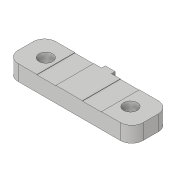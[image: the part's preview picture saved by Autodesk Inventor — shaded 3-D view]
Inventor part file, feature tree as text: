
AUTODESK INVENTOR PART (.ipt)
format: ipt  version: 2020 (Build 240168000, 168)  size: 139,776 bytes
history: native  units: in
note: dims shown in document units (in); Inventor stores cm internally (conversion verified against a paired STEP export)
features: extrude x5, sketch x5, mirror x2, plane x1, fillet x1
ambient origin geometry x8: Origin, YZ Plane, XZ Plane, XY Plane, X Axis, Y Axis, Z Axis, Center Point
bodies: Solid1 (feature_tree)
feature tree (14):
  extrude  "Extrusion1"  Depth=0.3937in
  extrude  "Extrusion2"  Depth=0.1575in TaperAngle=0.0deg
  plane  "Work Plane1"
  mirror  "Mirror1"
  fillet  "Fillet1"  [1 undecoded]
  extrude  "Extrusion3"  Depth=0.1181in
  extrude  "Extrusion4"  Depth=0.3937in
  mirror  "Mirror2"
  extrude  "Extrusion6"  Depth=0.315in
  sketch  "Sketch1"  dims[d0=1.2992in d1=0.3937in]
  sketch  "Sketch2"  dims[d2=0.1575in d3=0.0in d5=0.1575in d6=0.0in d7=-0.6496in]
  sketch  "Sketch3"  dims[d8=0.1181in d9=0.1417in]
  sketch  "Sketch4"  dims[d10=0.2756in d11=0.3937in]
  sketch  "Sketch6"  dims[d12=0.0039in d13=0.0in d14=0.315in d15=0.3937in d16=0.1181in d17=0.0039in d18=0.0in d21=0.3937in d22=0.0in d19=0.0197in d20=0.0344in]
note: 1 required parameter value undecoded (feature->parameter linkage not recoverable at this tier; creation-order binding heuristic only, values carry confidence <= 0.55)
